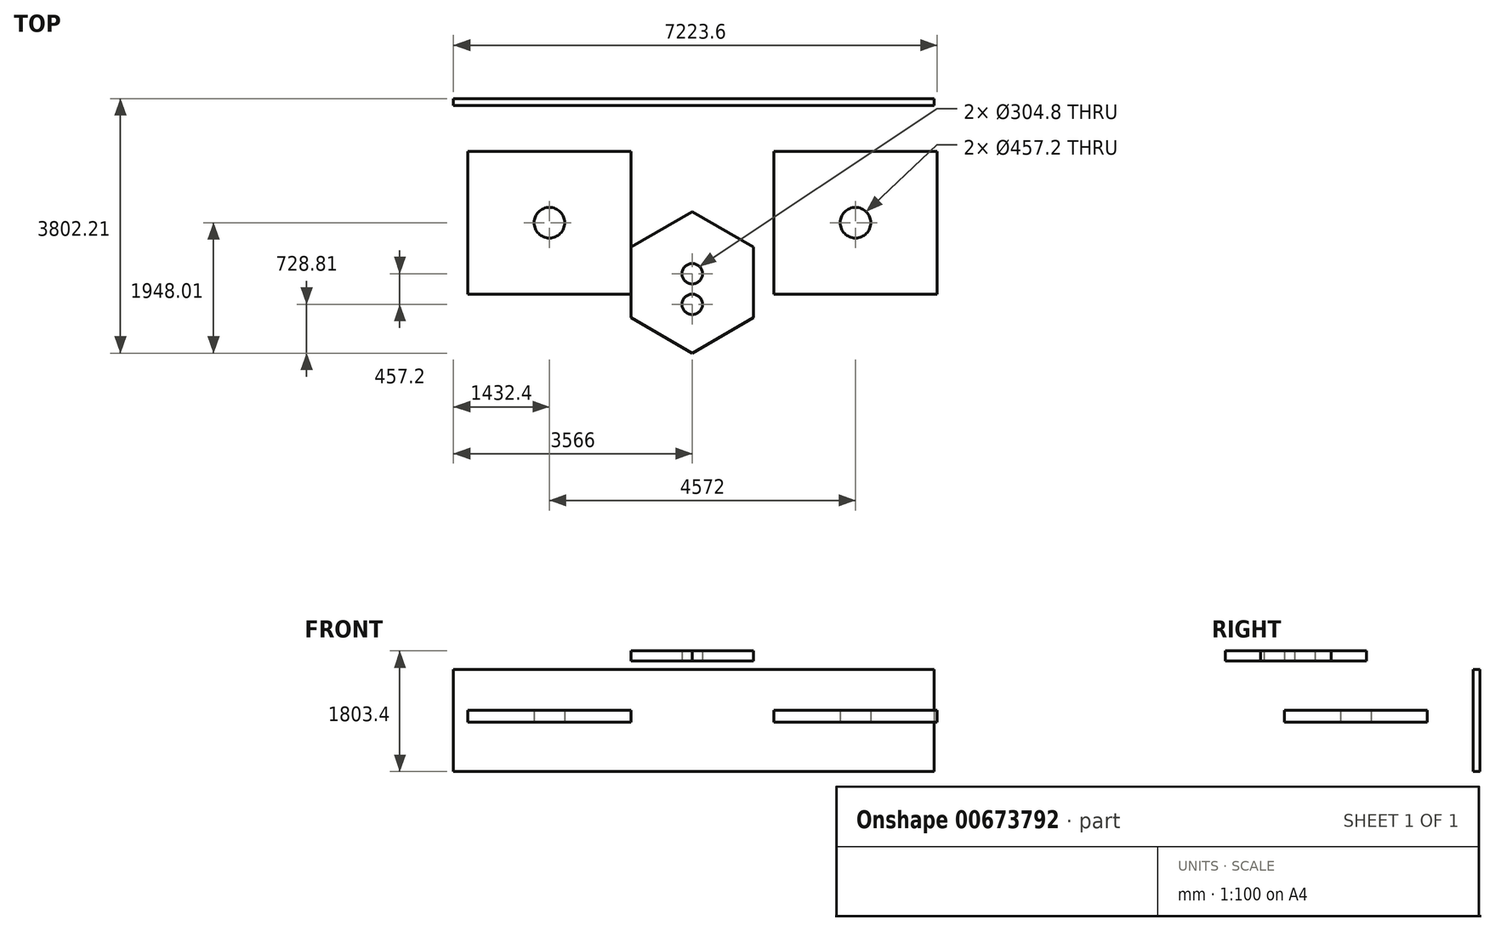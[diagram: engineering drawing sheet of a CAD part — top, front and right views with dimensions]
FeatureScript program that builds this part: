
annotation { "Feature Type Name" : "Feature", "Feature Type Description" : "" }
export const myFeature = defineFeature(function(context is Context, id is Id, definition is map)
    precondition{}
    {
        {
            var Q0;
            Q0=qCreatedBy(makeId("Top.planeOp"),FACE);
            var sketch = newSketch(context, id + "F0", { "sketchPlane" : qUnion([Q0])});
            skCircle(sketch, "E0", {"center": v(2438.4, 0) * mm, "radius": 228.6 * mm});
            skCircle(sketch, "E1", {"center": v(-2133.6, 0) * mm, "radius": 228.6 * mm});
            skCircle(sketch, "E2", {"center": v(0, -762) * mm, "radius": 152.4 * mm});
            skCircle(sketch, "E3", {"center": v(0, -1219.2) * mm, "radius": 152.4 * mm});
            skPoint(sketch, "E4.0.midPoint", {"position": v(-1206.7, 528.12) * mm});
            skCircle(sketch, "E5.cCircle", {"center": v(0, -892.15) * mm, "radius": 914.4 * mm, "construction": true});
            skLineSegment(sketch, "E5.0", {"start": v(0, 163.7) * mm, "end": v(914.4, -364.22) * mm});
            skLineSegment(sketch, "E5.1", {"start": v(914.4, -364.22) * mm, "end": v(914.4, -1420.08) * mm});
            skLineSegment(sketch, "E5.2", {"start": v(914.4, -1420.08) * mm, "end": v(0, -1948.01) * mm});
            skLineSegment(sketch, "E5.3", {"start": v(0, -1948.01) * mm, "end": v(-914.4, -1420.08) * mm});
            skLineSegment(sketch, "E5.4", {"start": v(-914.4, -1420.08) * mm, "end": v(-914.4, -364.22) * mm});
            skLineSegment(sketch, "E5.5", {"start": v(-914.4, -364.22) * mm, "end": v(0, 163.7) * mm});
            skPoint(sketch, "E5.0.midPoint", {"position": v(457.2, -100.26) * mm});
            skLineSegment(sketch, "E6.bottom", {"start": v(-2948.14, 1035.5) * mm, "end": v(-1424.14, 1035.5) * mm});
            skLineSegment(sketch, "E6.top", {"start": v(-2948.14, 324.3) * mm, "end": v(-1424.14, 324.3) * mm});
            skLineSegment(sketch, "E6.left", {"start": v(-2948.14, 1035.5) * mm, "end": v(-2948.14, 324.3) * mm});
            skLineSegment(sketch, "E6.right", {"start": v(-1424.14, 1035.5) * mm, "end": v(-1424.14, 324.3) * mm});
            skLineSegment(sketch, "E7.bottom", {"start": v(-914.4, 1066.8) * mm, "end": v(-3352.8, 1066.8) * mm});
            skLineSegment(sketch, "E7.left", {"start": v(-914.4, 1066.8) * mm, "end": v(-914.4, -1066.8) * mm});
            skLineSegment(sketch, "E7.right", {"start": v(-3352.8, 1066.8) * mm, "end": v(-3352.8, -1066.8) * mm});
            skLineSegment(sketch, "E8", {"start": v(-3352.8, -1066.8) * mm, "end": v(-914.4, -1066.8) * mm});
            skLineSegment(sketch, "E9.bottom", {"start": v(3657.6, 1066.8) * mm, "end": v(1219.2, 1066.8) * mm});
            skLineSegment(sketch, "E9.top", {"start": v(3657.6, -1066.8) * mm, "end": v(1219.2, -1066.8) * mm});
            skLineSegment(sketch, "E9.left", {"start": v(3657.6, 1066.8) * mm, "end": v(3657.6, -1066.8) * mm});
            skLineSegment(sketch, "E9.right", {"start": v(1219.2, 1066.8) * mm, "end": v(1219.2, -1066.8) * mm});
            skLineSegment(sketch, "E10", {"start": v(-914.4, 914.4) * mm, "end": v(1219.2, 914.4) * mm});
            skLineSegment(sketch, "E11", {"start": v(-914.4, 304.8) * mm, "end": v(1219.2, 304.8) * mm});
            skLineSegment(sketch, "E12", {"start": v(-914.4, -950.4) * mm, "end": v(-914.4, -950.4) * mm});
            skLineSegment(sketch, "E13", {"start": v(-914.4, -391.6) * mm, "end": v(-914.4, -391.6) * mm});
            skLineSegment(sketch, "E14", {"start": v(1219.2, -997.5) * mm, "end": v(914.4, -997.5) * mm});
            skLineSegment(sketch, "E15", {"start": v(1219.2, -484.22) * mm, "end": v(914.4, -484.22) * mm});
            skLineSegment(sketch, "E16", {"start": v(-1226.93, 914.4) * mm, "end": v(-1226.93, 304.8) * mm});
            skLineSegment(sketch, "E17.1.0.0", {"start": v(-1074.53, 914.4) * mm, "end": v(-1074.53, 304.8) * mm});
            skLineSegment(sketch, "E17.2.0.0", {"start": v(-922.13, 914.4) * mm, "end": v(-922.13, 304.8) * mm});
            skLineSegment(sketch, "E17.direction1", {"start": v(-1226.93, 304.8) * mm, "end": v(-1074.53, 304.8) * mm, "construction": true});
            skLineSegment(sketch, "E18.0.3.0", {"start": v(-769.73, 914.4) * mm, "end": v(-769.73, 304.8) * mm});
            skLineSegment(sketch, "E18.0.4.0", {"start": v(-617.33, 914.4) * mm, "end": v(-617.33, 304.8) * mm});
            skLineSegment(sketch, "E18.0.5.0", {"start": v(-464.93, 914.4) * mm, "end": v(-464.93, 304.8) * mm});
            skLineSegment(sketch, "E18.0.6.0", {"start": v(-312.53, 914.4) * mm, "end": v(-312.53, 304.8) * mm});
            skLineSegment(sketch, "E18.0.7.0", {"start": v(-160.13, 914.4) * mm, "end": v(-160.13, 304.8) * mm});
            skLineSegment(sketch, "E18.0.8.0", {"start": v(-7.73, 914.4) * mm, "end": v(-7.73, 304.8) * mm});
            skLineSegment(sketch, "E18.0.9.0", {"start": v(144.67, 914.4) * mm, "end": v(144.67, 304.8) * mm});
            skLineSegment(sketch, "E18.0.10.0", {"start": v(297.07, 914.4) * mm, "end": v(297.07, 304.8) * mm});
            skLineSegment(sketch, "E18.0.11.0", {"start": v(449.47, 914.4) * mm, "end": v(449.47, 304.8) * mm});
            skLineSegment(sketch, "E18.0.12.0", {"start": v(601.87, 914.4) * mm, "end": v(601.87, 304.8) * mm});
            skLineSegment(sketch, "E18.0.13.0", {"start": v(754.27, 914.4) * mm, "end": v(754.27, 304.8) * mm});
            skLineSegment(sketch, "E18.0.14.0", {"start": v(906.67, 914.4) * mm, "end": v(906.67, 304.8) * mm});
            skLineSegment(sketch, "E18.0.15.0", {"start": v(1059.07, 914.4) * mm, "end": v(1059.07, 304.8) * mm});
            skLineSegment(sketch, "E18.0.16.0", {"start": v(1211.47, 914.4) * mm, "end": v(1211.47, 304.8) * mm});
            skLineSegment(sketch, "E18.0.17.0", {"start": v(1363.87, 914.4) * mm, "end": v(1363.87, 304.8) * mm});
            skLineSegment(sketch, "E19.bottom", {"start": v(3260.76, 954.3) * mm, "end": v(2715.57, 954.3) * mm});
            skLineSegment(sketch, "E19.top", {"start": v(3260.76, -944.25) * mm, "end": v(2715.57, -944.25) * mm});
            skLineSegment(sketch, "E19.left", {"start": v(3260.76, 954.3) * mm, "end": v(3260.76, -944.25) * mm});
            skLineSegment(sketch, "E19.right", {"start": v(2715.57, 954.3) * mm, "end": v(2715.57, -944.25) * mm});
            skLineSegment(sketch, "E20.bottom", {"start": v(-3566, 1752.6) * mm, "end": v(3612.93, 1752.6) * mm});
            skLineSegment(sketch, "E20.top", {"start": v(-3566, 1854.2) * mm, "end": v(3612.93, 1854.2) * mm});
            skLineSegment(sketch, "E20.left", {"start": v(-3566, 1752.6) * mm, "end": v(-3566, 1854.2) * mm});
            skLineSegment(sketch, "E20.right", {"start": v(3612.93, 1752.6) * mm, "end": v(3612.93, 1854.2) * mm});
            skSolve(sketch);
        }
        {
            var Q0;
            Q0=sQuery(id+"F0.wireOp",EDGE,"E0");
            var Q1;
            Q1=sQuery(id+"F0.wireOp",EDGE,"E2");
            var Q2;
            Q2=sQuery(id+"F0.wireOp",EDGE,"E3");
            var Q3;
            Q3=sQuery(id+"F0.wireOp",EDGE,"E1");
            extrude(context, id + "F1", {"bodyType" : ToolBodyType.SURFACE, "surfaceEntities" : qUnion([Q0, Q1, Q2, Q3]), "oppositeDirection" : true, "depth" : 762 * mm, "offsetDistance" : 25.4 * mm});
        }
        {
            var Q0;
            Q0=makeQuery(id+"F0.imprint","IMPRINT",FACE,{"disambiguationData":[TD([[makeQuery(id+"F0.imprint","IMPRINT",EDGE,{"derivedFrom":sQuery(id+"F0.wireOp",EDGE,"E0")}),-1.0]])]});
            var Q1;
            Q1=makeQuery(id+"F0.imprint","IMPRINT",FACE,{"disambiguationData":[TD([[makeQuery(id+"F0.imprint","IMPRINT",EDGE,{"derivedFrom":sQuery(id+"F0.wireOp",EDGE,"E19.bottom")}),1.0]])]});
            var Q2;
            Q2=makeQuery(id+"F0.imprint","IMPRINT",FACE,{"disambiguationData":[TD([[makeQuery(id+"F0.imprint","IMPRINT",EDGE,{"derivedFrom":sQuery(id+"F0.wireOp",EDGE,"E1")}),-1.0]])]});
            var Q3;
            Q3=makeQuery(id+"F0.imprint","IMPRINT",FACE,{"disambiguationData":[TD([[makeQuery(id+"F0.imprint","IMPRINT",EDGE,{"derivedFrom":sQuery(id+"F0.wireOp",EDGE,"E6.bottom")}),-1.0]])]});
            extrude(context, id + "F2", {"entities" : qUnion([Q0, Q1, Q2, Q3]), "depth" : 177.8 * mm, "offsetDistance" : 25.4 * mm});
        }
        {
            var Q0;
            Q0=sQuery(id+"F0.wireOp",EDGE,"E1");
            var Q1;
            Q1=sQuery(id+"F0.wireOp",EDGE,"E0");
            var Q2;
            Q2=sQuery(id+"F0.wireOp",EDGE,"E2");
            var Q3;
            Q3=sQuery(id+"F0.wireOp",EDGE,"E3");
            extrude(context, id + "F3", {"bodyType" : ToolBodyType.SURFACE, "surfaceEntities" : qUnion([Q0, Q1, Q2, Q3]), "depth" : 2133.6 * mm, "offsetDistance" : 25.4 * mm});
        }
        {
            var Q0;
            Q0=makeQuery(id+"F0.imprint","IMPRINT",FACE,{"disambiguationData":[TD([[makeQuery(id+"F0.imprint","IMPRINT",EDGE,{"derivedFrom":sQuery(id+"F0.wireOp",EDGE,"E2")}),-1.0]])]});
            extrude(context, id + "F4", {"entities" : qUnion([Q0]), "depth" : 1066.8 * mm, "offsetDistance" : 25.4 * mm});
        }
        {
            var Q0;
            Q0=makeQuery(id+"F0.imprint","IMPRINT",FACE,{"disambiguationData":[TD([[makeQuery(id+"F0.imprint","IMPRINT",EDGE,{"derivedFrom":sQuery(id+"F0.wireOp",EDGE,"E2")}),-1.0]])]});
            extrude(context, id + "F5", {"entities" : qUnion([Q0]), "operationType" : NewBodyOperationType.REMOVE, "depth" : 914.4 * mm, "offsetDistance" : 25.4 * mm});
        }
        {
            var Q0;
            Q0=makeQuery(id+"F0.imprint","IMPRINT",FACE,{"disambiguationData":[TD([[makeQuery(id+"F0.imprint","IMPRINT",EDGE,{"derivedFrom":sQuery(id+"F0.wireOp",EDGE,"E20.bottom")}),1.0]])]});
            extrude(context, id + "F6", {"entities" : qUnion([Q0]), "depth" : 787.4 * mm, "offsetDistance" : 25.4 * mm, "hasSecondDirection" : true, "secondDirectionOppositeDirection" : true, "secondDirectionDepth" : 736.6 * mm});
        }
    });
